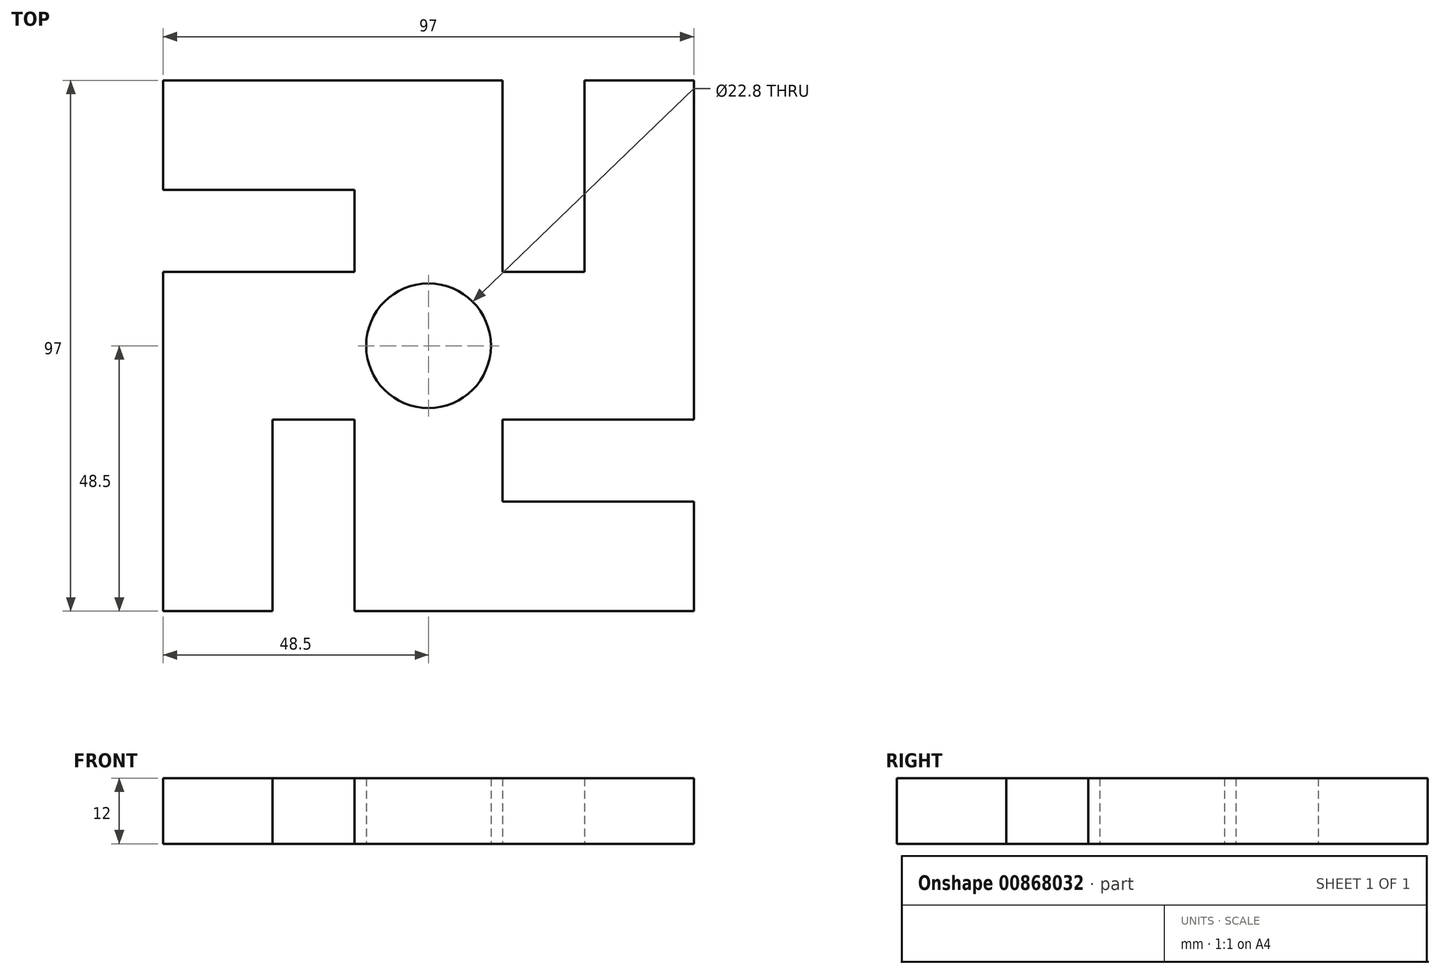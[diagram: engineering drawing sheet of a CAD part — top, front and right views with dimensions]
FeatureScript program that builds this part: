
annotation { "Feature Type Name" : "Feature", "Feature Type Description" : "" }
export const myFeature = defineFeature(function(context is Context, id is Id, definition is map)
    precondition{}
    {
        {
            var Q0;
            Q0=qCreatedBy(makeId("Top.planeOp"),FACE);
            var sketch = newSketch(context, id + "F0", { "sketchPlane" : qUnion([Q0])});
            skCircle(sketch, "E0", {"center": v(0, 0) * mm, "radius": 11.4 * mm});
            skLineSegment(sketch, "E1.bottom", {"start": v(13.5, 13.5) * mm, "end": v(-13.5, 13.5) * mm});
            skLineSegment(sketch, "E1.top", {"start": v(13.5, -13.5) * mm, "end": v(-13.5, -13.5) * mm});
            skLineSegment(sketch, "E1.left", {"start": v(13.5, 13.5) * mm, "end": v(13.5, -13.5) * mm});
            skLineSegment(sketch, "E1.right", {"start": v(-13.5, 13.5) * mm, "end": v(-13.5, -13.5) * mm});
            skLineSegment(sketch, "E2", {"start": v(-13.5, 13.5) * mm, "end": v(-13.5, 48.5) * mm});
            skLineSegment(sketch, "E3", {"start": v(-13.5, 48.5) * mm, "end": v(13.5, 48.5) * mm});
            skLineSegment(sketch, "E4", {"start": v(13.5, 48.5) * mm, "end": v(13.5, 13.5) * mm});
            skLineSegment(sketch, "E5", {"start": v(13.5, 13.5) * mm, "end": v(48.5, 13.5) * mm});
            skLineSegment(sketch, "E6", {"start": v(48.5, 13.5) * mm, "end": v(48.5, -13.5) * mm});
            skLineSegment(sketch, "E7", {"start": v(48.5, -13.5) * mm, "end": v(13.5, -13.5) * mm});
            skLineSegment(sketch, "E8", {"start": v(13.5, -13.5) * mm, "end": v(13.5, -48.5) * mm});
            skLineSegment(sketch, "E9", {"start": v(13.5, -48.5) * mm, "end": v(-13.5, -48.5) * mm});
            skLineSegment(sketch, "E10", {"start": v(-13.5, -48.5) * mm, "end": v(-13.5, -13.5) * mm});
            skLineSegment(sketch, "E11", {"start": v(-13.5, 13.5) * mm, "end": v(-48.5, 13.5) * mm});
            skLineSegment(sketch, "E12", {"start": v(-48.5, 13.5) * mm, "end": v(-48.5, -13.5) * mm});
            skLineSegment(sketch, "E13", {"start": v(-48.5, -13.5) * mm, "end": v(-13.5, -13.5) * mm});
            skLineSegment(sketch, "E14", {"start": v(-13.5, 48.5) * mm, "end": v(-48.5, 48.5) * mm});
            skLineSegment(sketch, "E15", {"start": v(-48.5, 48.5) * mm, "end": v(-48.5, 28.5) * mm});
            skLineSegment(sketch, "E16", {"start": v(-48.5, 28.5) * mm, "end": v(-13.5, 28.5) * mm});
            skLineSegment(sketch, "E17", {"start": v(48.5, 13.5) * mm, "end": v(48.5, 48.5) * mm});
            skLineSegment(sketch, "E18", {"start": v(48.5, 48.5) * mm, "end": v(28.5, 48.5) * mm});
            skLineSegment(sketch, "E19", {"start": v(28.5, 48.5) * mm, "end": v(28.5, 13.5) * mm});
            skPoint(sketch, "E19.endSnap0", {"position": v(31, 13.5) * mm});
            skLineSegment(sketch, "E20", {"start": v(13.5, -48.5) * mm, "end": v(48.5, -48.5) * mm});
            skLineSegment(sketch, "E21", {"start": v(48.5, -48.5) * mm, "end": v(48.5, -28.5) * mm});
            skLineSegment(sketch, "E22", {"start": v(48.5, -28.5) * mm, "end": v(13.5, -28.5) * mm});
            skLineSegment(sketch, "E23", {"start": v(-48.5, -13.5) * mm, "end": v(-48.5, -48.5) * mm});
            skLineSegment(sketch, "E24", {"start": v(-48.5, -48.5) * mm, "end": v(-28.5, -48.5) * mm});
            skLineSegment(sketch, "E25", {"start": v(-28.5, -48.5) * mm, "end": v(-28.5, -13.5) * mm});
            skPoint(sketch, "E25.endSnap0", {"position": v(-31, -13.5) * mm});
            skSolve(sketch);
        }
        {
            var Q0;
            {var subQ0=sQuery(id+"F0.wireOp",EDGE,"E14");Q0=makeQuery(id+"F0.imprint","IMPRINT",FACE,{"disambiguationData":[TD([[makeQuery(id+"F0.imprint","IMPRINT",EDGE,{"derivedFrom":subQ0}),1.0]])]});}
            var Q1;
            {var subQ2=sQuery(id+"F0.wireOp",EDGE,"E1.bottom");Q1=makeQuery(id+"F0.imprint","IMPRINT",FACE,{"disambiguationData":[TD([[makeQuery(id+"F0.imprint","IMPRINT",EDGE,{"derivedFrom":subQ2}),-1.0]])]});}
            var Q2;
            {var subQ0=sQuery(id+"F0.wireOp",EDGE,"E17");Q2=makeQuery(id+"F0.imprint","IMPRINT",FACE,{"disambiguationData":[TD([[makeQuery(id+"F0.imprint","IMPRINT",EDGE,{"derivedFrom":subQ0}),1.0]])]});}
            var Q3;
            {var subQ3=sQuery(id+"F0.wireOp",EDGE,"E1.left");Q3=makeQuery(id+"F0.imprint","IMPRINT",FACE,{"disambiguationData":[TD([[makeQuery(id+"F0.imprint","IMPRINT",EDGE,{"derivedFrom":subQ3}),1.0]])]});}
            var Q4;
            {var subQ3=sQuery(id+"F0.wireOp",EDGE,"E1.right");Q4=makeQuery(id+"F0.imprint","IMPRINT",FACE,{"disambiguationData":[TD([[makeQuery(id+"F0.imprint","IMPRINT",EDGE,{"derivedFrom":subQ3}),-1.0]])]});}
            var Q5;
            Q5=makeQuery(id+"F0.imprint","IMPRINT",FACE,{"disambiguationData":[TD([[makeQuery(id+"F0.imprint","IMPRINT",EDGE,{"derivedFrom":sQuery(id+"F0.wireOp",EDGE,"E0")}),-1.0]])]});
            var Q6;
            {var subQ3=sQuery(id+"F0.wireOp",EDGE,"E1.top");Q6=makeQuery(id+"F0.imprint","IMPRINT",FACE,{"disambiguationData":[TD([[makeQuery(id+"F0.imprint","IMPRINT",EDGE,{"derivedFrom":subQ3}),1.0]])]});}
            var Q7;
            {var subQ0=sQuery(id+"F0.wireOp",EDGE,"E23");Q7=makeQuery(id+"F0.imprint","IMPRINT",FACE,{"disambiguationData":[TD([[makeQuery(id+"F0.imprint","IMPRINT",EDGE,{"derivedFrom":subQ0}),1.0]])]});}
            var Q8;
            {var subQ0=sQuery(id+"F0.wireOp",EDGE,"E20");Q8=makeQuery(id+"F0.imprint","IMPRINT",FACE,{"disambiguationData":[TD([[makeQuery(id+"F0.imprint","IMPRINT",EDGE,{"derivedFrom":subQ0}),1.0]])]});}
            extrude(context, id + "F1", {"entities" : qUnion([Q0, Q1, Q2, Q3, Q4, Q5, Q6, Q7, Q8]), "depth" : 12 * mm, "offsetDistance" : 25 * mm});
        }
    });
